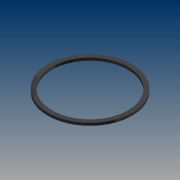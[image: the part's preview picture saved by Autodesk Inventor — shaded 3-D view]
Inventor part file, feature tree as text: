
AUTODESK INVENTOR PART (.ipt)
format: ipt  version: 2015 (Build 190159000, 159)  size: 77,312 bytes
history: native  units: mm
features: extrude x1, sketch x1
ambient origin geometry x8: Origin, YZ Plane, XZ Plane, XY Plane, X Axis, Y Axis, Z Axis, Center Point
bodies: Solid1 (feature_tree)
feature tree (2):
  extrude  "Extrusion1"  Depth=2.5mm
  sketch  "Sketch1"  dims[d0=80.0mm d1=72.0mm d2=2.5mm d3=0.0mm]
